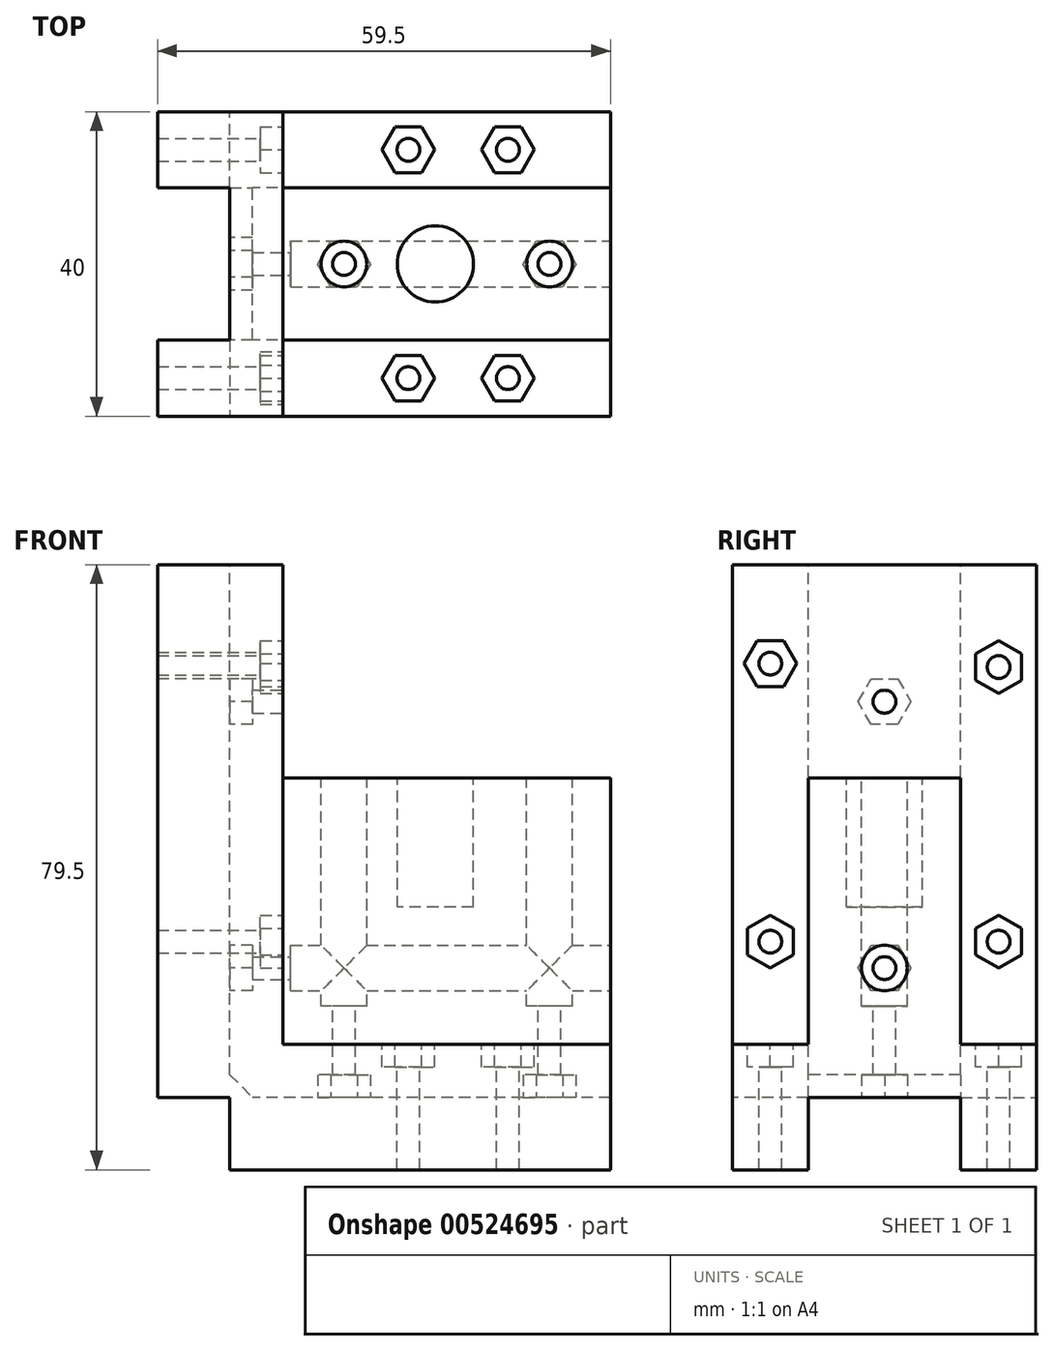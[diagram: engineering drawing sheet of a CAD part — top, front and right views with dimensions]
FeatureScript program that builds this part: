
annotation { "Feature Type Name" : "Feature", "Feature Type Description" : "" }
export const myFeature = defineFeature(function(context is Context, id is Id, definition is map)
    precondition{}
    {
        {
            var Q0;
            Q0=qCreatedBy(makeId("Front.planeOp"),FACE);
            var sketch = newSketch(context, id + "F0", { "sketchPlane" : qUnion([Q0])});
            skLineSegment(sketch, "E0", {"start": v(-50, 89.2) * mm, "end": v(-50, 19.2) * mm});
            skLineSegment(sketch, "E1", {"start": v(-50, 19.2) * mm, "end": v(0, 19.2) * mm});
            skLineSegment(sketch, "E2", {"start": v(0, 19.2) * mm, "end": v(0, 61.2) * mm});
            skLineSegment(sketch, "E3", {"start": v(0, 61.2) * mm, "end": v(-43, 61.2) * mm});
            skLineSegment(sketch, "E4", {"start": v(-43, 61.2) * mm, "end": v(-43, 89.2) * mm});
            skLineSegment(sketch, "E5", {"start": v(-43, 89.2) * mm, "end": v(-50, 89.2) * mm});
            skSolve(sketch);
        }
        {
            var Q0;
            Q0 = qSketchRegion(id + "F0", true);
            extrude(context, id + "F1", {"entities" : qUnion([Q0]), "depth" : 20 * mm, "offsetDistance" : 25 * mm});
        }
        {
            var Q0;
            Q0=makeQuery(id+"F1.opExtrude","CAP_FACE",FACE,{"disambiguationData":[OSD([sQuery(id+"F0.wireOp",EDGE,"E0"),sQuery(id+"F0.wireOp",EDGE,"E1"),sQuery(id+"F0.wireOp",EDGE,"E2"),sQuery(id+"F0.wireOp",EDGE,"E3"),sQuery(id+"F0.wireOp",EDGE,"E4"),sQuery(id+"F0.wireOp",EDGE,"E5")])],"isStart":false});
            var sketch = newSketch(context, id + "F2", { "sketchPlane" : qUnion([Q0])});
            skLineSegment(sketch, "E6", {"start": v(-50, 26.2) * mm, "end": v(0, 26.2) * mm});
            skSolve(sketch);
        }
        {
            var Q0;
            {var subQ0=sQuery(id+"F2.wireOp",EDGE,"E6");Q0=makeQuery(id+"F2.imprint","IMPRINT",FACE,{"disambiguationData":[TD([[makeQuery(id+"F2.imprint","IMPRINT",EDGE,{"derivedFrom":subQ0}),-1.0]])]});}
            extrude(context, id + "F3", {"entities" : qUnion([Q0]), "operationType" : NewBodyOperationType.ADD, "depth" : 10 * mm, "offsetDistance" : 25 * mm});
        }
        {
            var Q0;
            Q0=makeQuery(id+"F1.opExtrude","CAP_FACE",FACE,{"disambiguationData":[OSD([sQuery(id+"F0.wireOp",EDGE,"E0"),sQuery(id+"F0.wireOp",EDGE,"E1"),sQuery(id+"F0.wireOp",EDGE,"E2"),sQuery(id+"F0.wireOp",EDGE,"E3"),sQuery(id+"F0.wireOp",EDGE,"E4"),sQuery(id+"F0.wireOp",EDGE,"E5")])],"isStart":true});
            var sketch = newSketch(context, id + "F4", { "sketchPlane" : qUnion([Q0])});
            skLineSegment(sketch, "E7", {"start": v(0, 26.2) * mm, "end": v(50, 26.2) * mm});
            skSolve(sketch);
        }
        {
            var Q0;
            {var subQ0=sQuery(id+"F4.wireOp",EDGE,"E7");Q0=makeQuery(id+"F4.imprint","IMPRINT",FACE,{"disambiguationData":[TD([[makeQuery(id+"F4.imprint","IMPRINT",EDGE,{"derivedFrom":subQ0}),-1.0]])]});}
            extrude(context, id + "F5", {"entities" : qUnion([Q0]), "operationType" : NewBodyOperationType.ADD, "depth" : 10 * mm, "offsetDistance" : 25 * mm});
        }
        {
            var Q0;
            {var subQ0=sQuery(id+"F0.wireOp",EDGE,"E1");Q0=makeQuery(id+"F5.boolean.opBoolean","MERGE",FACE,{"derivedFrom":[makeQuery(id+"F3.boolean.opBoolean","MERGE",FACE,{"derivedFrom":[makeQuery(id+"F1.opExtrude","SWEPT_FACE",FACE,{"disambiguationData":[OSD([subQ0])]}),makeQuery(id+"F3.opExtrude","SWEPT_FACE",FACE,{"disambiguationData":[OSD([subQ0])]})]}),makeQuery(id+"F5.opExtrude","SWEPT_FACE",FACE,{"disambiguationData":[OSD([subQ0])]})]});}
            var sketch = newSketch(context, id + "F6", { "sketchPlane" : qUnion([Q0])});
            skLineSegment(sketch, "E8", {"start": v(0, 20) * mm, "end": v(-50, 20) * mm});
            skLineSegment(sketch, "E9", {"start": v(0, 0) * mm, "end": v(-50, 0) * mm});
            skSolve(sketch);
        }
        {
            var Q0;
            {var subQ0=sQuery(id+"F6.wireOp",EDGE,"E8");Q0=makeQuery(id+"F6.imprint","IMPRINT",FACE,{"disambiguationData":[TD([[makeQuery(id+"F6.imprint","IMPRINT",EDGE,{"derivedFrom":subQ0}),-1.0]])]});}
            var Q1;
            {var subQ0=sQuery(id+"F6.wireOp",EDGE,"E9");Q1=makeQuery(id+"F6.imprint","IMPRINT",FACE,{"disambiguationData":[TD([[makeQuery(id+"F6.imprint","IMPRINT",EDGE,{"derivedFrom":subQ0}),1.0]])]});}
            extrude(context, id + "F7", {"entities" : qUnion([Q0, Q1]), "operationType" : NewBodyOperationType.ADD, "depth" : 9.5 * mm, "offsetDistance" : 25 * mm});
        }
        {
            var Q0;
            Q0=makeQuery(id+"F5.opExtrude","SWEPT_FACE",FACE,{"disambiguationData":[OSD([sQuery(id+"F4.wireOp",EDGE,"E7")])]});
            var sketch = newSketch(context, id + "F8", { "sketchPlane" : qUnion([Q0])});
            skLineSegment(sketch, "E10", {"start": v(-30, -25) * mm, "end": v(-28.27, -28) * mm});
            skLineSegment(sketch, "E11", {"start": v(-28.27, -28) * mm, "end": v(-24.8, -28) * mm});
            skLineSegment(sketch, "E12", {"start": v(-24.8, -28) * mm, "end": v(-23.07, -25) * mm});
            skLineSegment(sketch, "E13", {"start": v(-23.07, -25) * mm, "end": v(-24.8, -22) * mm});
            skLineSegment(sketch, "E14", {"start": v(-24.8, -22) * mm, "end": v(-28.27, -22) * mm});
            skLineSegment(sketch, "E15", {"start": v(-28.27, -22) * mm, "end": v(-30, -25) * mm});
            skCircle(sketch, "E16", {"center": v(-26.54, -25) * mm, "radius": 1.5 * mm});
            skLineSegment(sketch, "E17", {"start": v(-16.93, -25) * mm, "end": v(-15.2, -28) * mm});
            skLineSegment(sketch, "E18", {"start": v(-15.2, -28) * mm, "end": v(-11.73, -28) * mm});
            skLineSegment(sketch, "E19", {"start": v(-11.73, -28) * mm, "end": v(-10, -25) * mm});
            skLineSegment(sketch, "E20", {"start": v(-10, -25) * mm, "end": v(-11.73, -22) * mm});
            skLineSegment(sketch, "E21", {"start": v(-11.73, -22) * mm, "end": v(-15.2, -22) * mm});
            skLineSegment(sketch, "E22", {"start": v(-15.2, -22) * mm, "end": v(-16.93, -25) * mm});
            skCircle(sketch, "E23", {"center": v(-13.46, -25) * mm, "radius": 1.5 * mm});
            skLineSegment(sketch, "E24", {"start": v(-30, 5) * mm, "end": v(-28.27, 2) * mm});
            skLineSegment(sketch, "E25", {"start": v(-28.27, 2) * mm, "end": v(-24.8, 2) * mm});
            skLineSegment(sketch, "E26", {"start": v(-24.8, 2) * mm, "end": v(-23.07, 5) * mm});
            skLineSegment(sketch, "E27", {"start": v(-23.07, 5) * mm, "end": v(-24.8, 8) * mm});
            skLineSegment(sketch, "E28", {"start": v(-24.8, 8) * mm, "end": v(-28.27, 8) * mm});
            skLineSegment(sketch, "E29", {"start": v(-28.27, 8) * mm, "end": v(-30, 5) * mm});
            skCircle(sketch, "E30", {"center": v(-26.54, 5) * mm, "radius": 1.5 * mm});
            skLineSegment(sketch, "E31", {"start": v(-16.93, 5) * mm, "end": v(-15.2, 2) * mm});
            skLineSegment(sketch, "E32", {"start": v(-15.2, 2) * mm, "end": v(-11.73, 2) * mm});
            skLineSegment(sketch, "E33", {"start": v(-11.73, 2) * mm, "end": v(-10, 5) * mm});
            skLineSegment(sketch, "E34", {"start": v(-10, 5) * mm, "end": v(-11.73, 8) * mm});
            skLineSegment(sketch, "E35", {"start": v(-11.73, 8) * mm, "end": v(-15.2, 8) * mm});
            skLineSegment(sketch, "E36", {"start": v(-15.2, 8) * mm, "end": v(-16.93, 5) * mm});
            skCircle(sketch, "E37", {"center": v(-13.46, 5) * mm, "radius": 1.5 * mm});
            skLineSegment(sketch, "E38", {"start": v(-43, 0) * mm, "end": v(-43, 10) * mm});
            skLineSegment(sketch, "E39.bottom", {"start": v(-43, -20) * mm, "end": v(-50, -20) * mm});
            skLineSegment(sketch, "E39.top", {"start": v(-43, -30) * mm, "end": v(-50, -30) * mm});
            skLineSegment(sketch, "E39.left", {"start": v(-43, -20) * mm, "end": v(-43, -30) * mm});
            skLineSegment(sketch, "E39.right", {"start": v(-50, -20) * mm, "end": v(-50, -30) * mm});
            skSolve(sketch);
        }
        {
            var Q0;
            Q0=makeQuery(id+"F8.imprint","IMPRINT",FACE,{"disambiguationData":[TD([[makeQuery(id+"F8.imprint","IMPRINT",EDGE,{"derivedFrom":sQuery(id+"F8.wireOp",EDGE,"E24")}),1.0]])]});
            var Q1;
            Q1=makeQuery(id+"F8.imprint","IMPRINT",FACE,{"disambiguationData":[TD([[makeQuery(id+"F8.imprint","IMPRINT",EDGE,{"derivedFrom":sQuery(id+"F8.wireOp",EDGE,"E31")}),1.0]])]});
            var Q2;
            Q2=makeQuery(id+"F8.imprint","IMPRINT",FACE,{"disambiguationData":[TD([[makeQuery(id+"F8.imprint","IMPRINT",EDGE,{"derivedFrom":sQuery(id+"F8.wireOp",EDGE,"E17")}),1.0]])]});
            var Q3;
            Q3=makeQuery(id+"F8.imprint","IMPRINT",FACE,{"disambiguationData":[TD([[makeQuery(id+"F8.imprint","IMPRINT",EDGE,{"derivedFrom":sQuery(id+"F8.wireOp",EDGE,"E10")}),1.0]])]});
            extrude(context, id + "F9", {"entities" : qUnion([Q0, Q1, Q2, Q3]), "operationType" : NewBodyOperationType.REMOVE, "oppositeDirection" : true, "depth" : 3 * mm, "offsetDistance" : 25 * mm});
        }
        {
            var Q0;
            Q0=makeQuery(id+"F9.boolean.opBoolean","SPLIT",FACE,{"disambiguationData":[TD([makeQuery(id+"F9.opExtrude","SWEPT_FACE",FACE,{"disambiguationData":[OSD([sQuery(id+"F8.wireOp",EDGE,"E30")])]})])],"derivedFrom":makeQuery(id+"F5.opExtrude","SWEPT_FACE",FACE,{"disambiguationData":[OSD([sQuery(id+"F4.wireOp",EDGE,"E7")])]})});
            var Q1;
            Q1=makeQuery(id+"F9.boolean.opBoolean","SPLIT",FACE,{"disambiguationData":[TD([makeQuery(id+"F9.opExtrude","SWEPT_FACE",FACE,{"disambiguationData":[OSD([sQuery(id+"F8.wireOp",EDGE,"E16")])]})])],"derivedFrom":makeQuery(id+"F3.opExtrude","SWEPT_FACE",FACE,{"disambiguationData":[OSD([sQuery(id+"F2.wireOp",EDGE,"E6")])]})});
            var Q2;
            Q2=makeQuery(id+"F9.boolean.opBoolean","SPLIT",FACE,{"disambiguationData":[TD([makeQuery(id+"F9.opExtrude","SWEPT_FACE",FACE,{"disambiguationData":[OSD([sQuery(id+"F8.wireOp",EDGE,"E23")])]})])],"derivedFrom":makeQuery(id+"F3.opExtrude","SWEPT_FACE",FACE,{"disambiguationData":[OSD([sQuery(id+"F2.wireOp",EDGE,"E6")])]})});
            var Q3;
            Q3=makeQuery(id+"F9.boolean.opBoolean","SPLIT",FACE,{"disambiguationData":[TD([makeQuery(id+"F9.opExtrude","SWEPT_FACE",FACE,{"disambiguationData":[OSD([sQuery(id+"F8.wireOp",EDGE,"E37")])]})])],"derivedFrom":makeQuery(id+"F5.opExtrude","SWEPT_FACE",FACE,{"disambiguationData":[OSD([sQuery(id+"F4.wireOp",EDGE,"E7")])]})});
            extrude(context, id + "F10", {"entities" : qUnion([Q0, Q1, Q2, Q3]), "operationType" : NewBodyOperationType.REMOVE, "oppositeDirection" : true, "depth" : 20 * mm, "offsetDistance" : 25 * mm});
        }
        {
            var Q0;
            {var subQ0=sQuery(id+"F8.wireOp",EDGE,"E38");Q0=makeQuery(id+"F8.imprint","IMPRINT",FACE,{"disambiguationData":[TD([[makeQuery(id+"F8.imprint","IMPRINT",EDGE,{"derivedFrom":subQ0}),1.0]])]});}
            var Q1;
            Q1=makeQuery(id+"F8.imprint","IMPRINT",FACE,{"disambiguationData":[TD([[makeQuery(id+"F8.imprint","IMPRINT",EDGE,{"derivedFrom":sQuery(id+"F8.wireOp",EDGE,"E39.bottom")}),1.0]])]});
            extrude(context, id + "F11", {"entities" : qUnion([Q0, Q1]), "operationType" : NewBodyOperationType.ADD, "depth" : 63 * mm, "offsetDistance" : 25 * mm});
        }
        {
            var Q0;
            {var subQ0=sQuery(id+"F0.wireOp",EDGE,"E0");var subQ1=sQuery(id+"F0.wireOp",EDGE,"E1");var subQ2=makeQuery(id+"F5.boolean.opBoolean","MERGE",EDGE,{"derivedFrom":[makeQuery(id+"F3.boolean.opBoolean","MERGE",EDGE,{"derivedFrom":[makeQuery(id+"F1.opExtrude","SWEPT_EDGE",EDGE,{"disambiguationData":[OSD([subQ0,subQ1])]}),makeQuery(id+"F3.opExtrude","SWEPT_EDGE",EDGE,{"disambiguationData":[OSD([subQ0,subQ1])]})]}),makeQuery(id+"F5.opExtrude","SWEPT_EDGE",EDGE,{"disambiguationData":[OSD([subQ0,subQ1])]})]});Q0=makeQuery(id+"F11.boolean.opBoolean","MERGE",FACE,{"derivedFrom":[makeQuery(id+"F7.boolean.opBoolean","MERGE",FACE,{"derivedFrom":[makeQuery(id+"F5.boolean.opBoolean","MERGE",FACE,{"derivedFrom":[makeQuery(id+"F3.boolean.opBoolean","MERGE",FACE,{"derivedFrom":[makeQuery(id+"F1.opExtrude","SWEPT_FACE",FACE,{"disambiguationData":[OSD([subQ0])]}),makeQuery(id+"F3.opExtrude","SWEPT_FACE",FACE,{"disambiguationData":[OSD([subQ0])]})]}),makeQuery(id+"F5.opExtrude","SWEPT_FACE",FACE,{"disambiguationData":[OSD([subQ0])]})]}),makeQuery(id+"F7.opExtrude","SWEPT_FACE",FACE,{"disambiguationData":[OSD([subQ0,subQ1]),TDD([makeQuery(id+"F6.imprint","IMPRINT",EDGE,{"disambiguationData":[TD([[makeQuery(id+"F6.imprint","INTERSECT",VERTEX,{"derivedFrom":[makeQuery(id+"F3.opExtrude","CAP_EDGE",EDGE,{"disambiguationData":[OSD([subQ1])],"isStart":false}),subQ2]}),-1.0]])],"derivedFrom":subQ2})])]}),makeQuery(id+"F7.opExtrude","SWEPT_FACE",FACE,{"disambiguationData":[OSD([subQ0,subQ1]),TDD([makeQuery(id+"F6.imprint","IMPRINT",EDGE,{"disambiguationData":[TD([[makeQuery(id+"F6.imprint","INTERSECT",VERTEX,{"derivedFrom":[makeQuery(id+"F5.opExtrude","CAP_EDGE",EDGE,{"disambiguationData":[OSD([subQ1])],"isStart":false}),subQ2]}),1.0]])],"derivedFrom":subQ2})])]})]}),makeQuery(id+"F11.opExtrude","SWEPT_FACE",FACE,{"disambiguationData":[OSD([sQuery(id+"F8.wireOp",EDGE,"E39.right")])]}),makeQuery(id+"F11.opExtrude","SWEPT_FACE",FACE,{"disambiguationData":[OSD([subQ0,sQuery(id+"F4.wireOp",EDGE,"E7")])]})]});}
            var sketch = newSketch(context, id + "F12", { "sketchPlane" : qUnion([Q0])});
            skLineSegment(sketch, "E40", {"start": v(20, 19.2) * mm, "end": v(20, 89.2) * mm});
            skLineSegment(sketch, "E41", {"start": v(0, 19.2) * mm, "end": v(0, 89.2) * mm});
            skLineSegment(sketch, "E42", {"start": v(20, 19.2) * mm, "end": v(30, 19.2) * mm});
            skLineSegment(sketch, "E43", {"start": v(0, 19.2) * mm, "end": v(-10, 19.2) * mm});
            skSolve(sketch);
        }
        {
            var Q0;
            {var subQ0=sQuery(id+"F12.wireOp",EDGE,"E40");Q0=makeQuery(id+"F12.imprint","IMPRINT",FACE,{"disambiguationData":[TD([[makeQuery(id+"F12.imprint","IMPRINT",EDGE,{"derivedFrom":subQ0}),-1.0]])]});}
            var Q1;
            {var subQ0=sQuery(id+"F12.wireOp",EDGE,"E41");Q1=makeQuery(id+"F12.imprint","IMPRINT",FACE,{"disambiguationData":[TD([[makeQuery(id+"F12.imprint","IMPRINT",EDGE,{"derivedFrom":subQ0}),1.0]])]});}
            extrude(context, id + "F13", {"entities" : qUnion([Q0, Q1]), "operationType" : NewBodyOperationType.ADD, "depth" : 9.5 * mm, "offsetDistance" : 25 * mm});
        }
        {
            var Q0;
            Q0=makeQuery(id+"F11.opExtrude","SWEPT_FACE",FACE,{"disambiguationData":[OSD([sQuery(id+"F8.wireOp",EDGE,"E39.left")])]});
            var sketch = newSketch(context, id + "F14", { "sketchPlane" : qUnion([Q0])});
            skLineSegment(sketch, "E44", {"start": v(-25, 43.12) * mm, "end": v(-28, 41.39) * mm});
            skLineSegment(sketch, "E45", {"start": v(-28, 41.39) * mm, "end": v(-28, 37.93) * mm});
            skLineSegment(sketch, "E46", {"start": v(-28, 37.93) * mm, "end": v(-25, 36.2) * mm});
            skLineSegment(sketch, "E47", {"start": v(-25, 36.2) * mm, "end": v(-22, 37.93) * mm});
            skLineSegment(sketch, "E48", {"start": v(-22, 37.93) * mm, "end": v(-22, 41.39) * mm});
            skLineSegment(sketch, "E49", {"start": v(-22, 41.39) * mm, "end": v(-25, 43.12) * mm});
            skCircle(sketch, "E50", {"center": v(-25, 39.66) * mm, "radius": 1.5 * mm});
            skLineSegment(sketch, "E51", {"start": v(5, 79.2) * mm, "end": v(2, 77.46) * mm});
            skLineSegment(sketch, "E52", {"start": v(2, 77.46) * mm, "end": v(2, 74) * mm});
            skLineSegment(sketch, "E53", {"start": v(2, 74) * mm, "end": v(5, 72.26) * mm});
            skLineSegment(sketch, "E54", {"start": v(5, 72.26) * mm, "end": v(8, 74) * mm});
            skLineSegment(sketch, "E55", {"start": v(8, 74) * mm, "end": v(8, 77.46) * mm});
            skLineSegment(sketch, "E56", {"start": v(8, 77.46) * mm, "end": v(5, 79.2) * mm});
            skCircle(sketch, "E57", {"center": v(5, 75.73) * mm, "radius": 1.5 * mm});
            skLineSegment(sketch, "E58", {"start": v(5, 43.12) * mm, "end": v(2, 41.39) * mm});
            skLineSegment(sketch, "E59", {"start": v(2, 41.39) * mm, "end": v(2, 37.93) * mm});
            skLineSegment(sketch, "E60", {"start": v(2, 37.93) * mm, "end": v(5, 36.2) * mm});
            skLineSegment(sketch, "E61", {"start": v(5, 36.2) * mm, "end": v(8, 37.93) * mm});
            skLineSegment(sketch, "E62", {"start": v(8, 37.93) * mm, "end": v(8, 41.39) * mm});
            skLineSegment(sketch, "E63", {"start": v(8, 41.39) * mm, "end": v(5, 43.12) * mm});
            skCircle(sketch, "E64", {"center": v(5, 39.66) * mm, "radius": 1.5 * mm});
            skLineSegment(sketch, "E65", {"start": v(-28.46, 76.2) * mm, "end": v(-26.73, 73.2) * mm});
            skLineSegment(sketch, "E66", {"start": v(-26.73, 73.2) * mm, "end": v(-23.27, 73.2) * mm});
            skLineSegment(sketch, "E67", {"start": v(-23.27, 73.2) * mm, "end": v(-21.54, 76.2) * mm});
            skLineSegment(sketch, "E68", {"start": v(-21.54, 76.2) * mm, "end": v(-23.27, 79.2) * mm});
            skLineSegment(sketch, "E69", {"start": v(-23.27, 79.2) * mm, "end": v(-26.73, 79.2) * mm});
            skLineSegment(sketch, "E70", {"start": v(-26.73, 79.2) * mm, "end": v(-28.46, 76.2) * mm});
            skCircle(sketch, "E71", {"center": v(-25, 76.2) * mm, "radius": 1.5 * mm});
            skSolve(sketch);
        }
        {
            var Q0;
            Q0=makeQuery(id+"F14.imprint","IMPRINT",FACE,{"disambiguationData":[TD([[makeQuery(id+"F14.imprint","IMPRINT",EDGE,{"derivedFrom":sQuery(id+"F14.wireOp",EDGE,"3def0d78-31c6-4fae-8652-5ddfac95fd14")}),1.0]])]});
            var Q1;
            Q1=makeQuery(id+"F14.imprint","IMPRINT",FACE,{"disambiguationData":[TD([[makeQuery(id+"F14.imprint","IMPRINT",EDGE,{"derivedFrom":sQuery(id+"F14.wireOp",EDGE,"E51")}),1.0]])]});
            var Q2;
            Q2=makeQuery(id+"F14.imprint","IMPRINT",FACE,{"disambiguationData":[TD([[makeQuery(id+"F14.imprint","IMPRINT",EDGE,{"derivedFrom":sQuery(id+"F14.wireOp",EDGE,"E44")}),1.0]])]});
            var Q3;
            Q3=makeQuery(id+"F14.imprint","IMPRINT",FACE,{"disambiguationData":[TD([[makeQuery(id+"F14.imprint","IMPRINT",EDGE,{"derivedFrom":sQuery(id+"F14.wireOp",EDGE,"E58")}),1.0]])]});
            var Q4;
            Q4 = qSketchRegion(id + "F17", true);
            var Q5;
            Q5=makeQuery(id+"F14.imprint","IMPRINT",FACE,{"disambiguationData":[TD([[makeQuery(id+"F14.imprint","IMPRINT",EDGE,{"derivedFrom":sQuery(id+"F14.wireOp",EDGE,"E65")}),1.0]])]});
            extrude(context, id + "F15", {"entities" : qUnion([Q0, Q1, Q2, Q3, Q4, Q5]), "operationType" : NewBodyOperationType.REMOVE, "oppositeDirection" : true, "depth" : 3 * mm, "offsetDistance" : 25 * mm});
        }
        {
            var Q0;
            Q0=makeQuery(id+"F15.boolean.opBoolean","SPLIT",FACE,{"disambiguationData":[TD([makeQuery(id+"F15.opExtrude","SWEPT_FACE",FACE,{"disambiguationData":[OSD([sQuery(id+"F14.wireOp",EDGE,"ef229b5c-997c-4e16-8a30-6795fe06fc26")])]})])],"derivedFrom":makeQuery(id+"F11.opExtrude","SWEPT_FACE",FACE,{"disambiguationData":[OSD([sQuery(id+"F8.wireOp",EDGE,"E39.left")])]})});
            var Q1;
            Q1=makeQuery(id+"F15.boolean.opBoolean","SPLIT",FACE,{"disambiguationData":[TD([makeQuery(id+"F15.opExtrude","SWEPT_FACE",FACE,{"disambiguationData":[OSD([sQuery(id+"F14.wireOp",EDGE,"E57")])]})])],"derivedFrom":makeQuery(id+"F11.opExtrude","SWEPT_FACE",FACE,{"disambiguationData":[OSD([sQuery(id+"F8.wireOp",EDGE,"E38")])]})});
            var Q2;
            Q2=makeQuery(id+"F15.boolean.opBoolean","SPLIT",FACE,{"disambiguationData":[TD([makeQuery(id+"F15.opExtrude","SWEPT_FACE",FACE,{"disambiguationData":[OSD([sQuery(id+"F14.wireOp",EDGE,"E64")])]})])],"derivedFrom":makeQuery(id+"F11.opExtrude","SWEPT_FACE",FACE,{"disambiguationData":[OSD([sQuery(id+"F8.wireOp",EDGE,"E38")])]})});
            var Q3;
            Q3=makeQuery(id+"F15.boolean.opBoolean","SPLIT",FACE,{"disambiguationData":[TD([makeQuery(id+"F15.opExtrude","SWEPT_FACE",FACE,{"disambiguationData":[OSD([sQuery(id+"F14.wireOp",EDGE,"E50")])]})])],"derivedFrom":makeQuery(id+"F11.opExtrude","SWEPT_FACE",FACE,{"disambiguationData":[OSD([sQuery(id+"F8.wireOp",EDGE,"E39.left")])]})});
            var Q4;
            Q4=makeQuery(id+"F15.boolean.opBoolean","SPLIT",FACE,{"disambiguationData":[TD([makeQuery(id+"F15.opExtrude","SWEPT_FACE",FACE,{"disambiguationData":[OSD([sQuery(id+"F14.wireOp",EDGE,"E71")])]})])],"derivedFrom":makeQuery(id+"F11.boolean.opBoolean","MERGE",FACE,{"derivedFrom":[makeQuery(id+"F1.opExtrude","SWEPT_FACE",FACE,{"disambiguationData":[OSD([sQuery(id+"F0.wireOp",EDGE,"E4")])]}),makeQuery(id+"F11.opExtrude","SWEPT_FACE",FACE,{"disambiguationData":[OSD([sQuery(id+"F8.wireOp",EDGE,"E38")])]}),makeQuery(id+"F11.opExtrude","SWEPT_FACE",FACE,{"disambiguationData":[OSD([sQuery(id+"F8.wireOp",EDGE,"E39.left")])]})]})});
            extrude(context, id + "F16", {"entities" : qUnion([Q0, Q1, Q2, Q3, Q4]), "operationType" : NewBodyOperationType.REMOVE, "oppositeDirection" : true, "depth" : 20 * mm, "offsetDistance" : 25 * mm});
        }
        {
            var Q0;
            Q0=makeQuery(id+"F1.opExtrude","SWEPT_FACE",FACE,{"disambiguationData":[OSD([sQuery(id+"F0.wireOp",EDGE,"E3")])]});
            var sketch = newSketch(context, id + "F17", { "sketchPlane" : qUnion([Q0])});
            skCircle(sketch, "E72", {"center": v(-23, -10) * mm, "radius": 5 * mm});
            skPoint(sketch, "E73", {"position": v(-8, -10) * mm});
            skPoint(sketch, "E74", {"position": v(-35, -10) * mm});
            skSolve(sketch);
        }
        {
            var Q0;
            Q0=makeQuery(id+"F17.imprint","IMPRINT",FACE,{"disambiguationData":[TD([[makeQuery(id+"F17.imprint","IMPRINT",EDGE,{"derivedFrom":sQuery(id+"F17.wireOp",EDGE,"E72")}),1.0]])]});
            extrude(context, id + "F18", {"entities" : qUnion([Q0]), "operationType" : NewBodyOperationType.REMOVE, "oppositeDirection" : true, "depth" : 17 * mm, "offsetDistance" : 25 * mm});
        }
        {
            var Q0;
            {var subQ0=sQuery(id+"F0.wireOp",EDGE,"E1");var subQ1=sQuery(id+"F0.wireOp",EDGE,"E0");Q0=makeQuery(id+"F5.boolean.opBoolean","MERGE",EDGE,{"derivedFrom":[makeQuery(id+"F3.boolean.opBoolean","MERGE",EDGE,{"derivedFrom":[makeQuery(id+"F1.opExtrude","SWEPT_EDGE",EDGE,{"disambiguationData":[OSD([subQ1,subQ0])]}),makeQuery(id+"F3.opExtrude","SWEPT_EDGE",EDGE,{"disambiguationData":[OSD([subQ1,subQ0])]})]}),makeQuery(id+"F5.opExtrude","SWEPT_EDGE",EDGE,{"disambiguationData":[OSD([subQ1,subQ0])]})]});}
            chamfer(context, id + "F19", {"entities" : qUnion([Q0]), "width" : 3 * mm, "tangentPropagation" : true});
        }
        {
            var Q0;
            Q0=sQuery(id+"F17.wireOp",VERTEX,"E73");
            var Q1;
            Q1=sQuery(id+"F17.wireOp",VERTEX,"E74");
            var Q2;
            Q2=makeQuery(id+"F1.opExtrude","SWEPT_BODY",BODY,{"disambiguationData":[OSD([sQuery(id+"F0.wireOp",EDGE,"E0"),sQuery(id+"F0.wireOp",EDGE,"E1"),sQuery(id+"F0.wireOp",EDGE,"E2"),sQuery(id+"F0.wireOp",EDGE,"E3"),sQuery(id+"F0.wireOp",EDGE,"E4"),sQuery(id+"F0.wireOp",EDGE,"E5")])]});
            hole(context, id + "F20", {"style" : HoleStyle.C_BORE, "endStyle" : HoleEndStyle.THROUGH, "holeDiameter" : 3 * mm, "cBoreDiameter" : 6 * mm, "cBoreDepth" : 30 * mm, "isTappedThrough" : true, "tappedDepth" : 12 * mm, "tapClearance" : 3, "startFromSketch" : true, "locations" : qUnion([Q0, Q1]), "scope" : qUnion([Q2])});
        }
        {
            var Q0;
            {var subQ0=sQuery(id+"F0.wireOp",EDGE,"E1");Q0=makeQuery(id+"F5.boolean.opBoolean","MERGE",FACE,{"derivedFrom":[makeQuery(id+"F3.boolean.opBoolean","MERGE",FACE,{"derivedFrom":[makeQuery(id+"F1.opExtrude","SWEPT_FACE",FACE,{"disambiguationData":[OSD([subQ0])]}),makeQuery(id+"F3.opExtrude","SWEPT_FACE",FACE,{"disambiguationData":[OSD([subQ0])]})]}),makeQuery(id+"F5.opExtrude","SWEPT_FACE",FACE,{"disambiguationData":[OSD([subQ0])]})]});}
            var sketch = newSketch(context, id + "F21", { "sketchPlane" : qUnion([Q0])});
            skLineSegment(sketch, "E75", {"start": v(-38.46, 10) * mm, "end": v(-36.73, 7) * mm});
            skLineSegment(sketch, "E76", {"start": v(-36.73, 7) * mm, "end": v(-33.27, 7) * mm});
            skLineSegment(sketch, "E77", {"start": v(-33.27, 7) * mm, "end": v(-31.54, 10) * mm});
            skLineSegment(sketch, "E78", {"start": v(-31.54, 10) * mm, "end": v(-33.27, 13) * mm});
            skLineSegment(sketch, "E79", {"start": v(-33.27, 13) * mm, "end": v(-36.73, 13) * mm});
            skLineSegment(sketch, "E80", {"start": v(-36.73, 13) * mm, "end": v(-38.46, 10) * mm});
            skCircle(sketch, "E81", {"center": v(-35, 10) * mm, "radius": 1.5 * mm});
            skLineSegment(sketch, "E82", {"start": v(-11.46, 10) * mm, "end": v(-9.73, 7) * mm});
            skLineSegment(sketch, "E83", {"start": v(-9.73, 7) * mm, "end": v(-6.27, 7) * mm});
            skLineSegment(sketch, "E84", {"start": v(-6.27, 7) * mm, "end": v(-4.54, 10) * mm});
            skLineSegment(sketch, "E85", {"start": v(-4.54, 10) * mm, "end": v(-6.27, 13) * mm});
            skLineSegment(sketch, "E86", {"start": v(-6.27, 13) * mm, "end": v(-9.73, 13) * mm});
            skLineSegment(sketch, "E87", {"start": v(-9.73, 13) * mm, "end": v(-11.46, 10) * mm});
            skCircle(sketch, "E88", {"center": v(-8, 10) * mm, "radius": 1.5 * mm});
            skSolve(sketch);
        }
        {
            var Q0;
            Q0=makeQuery(id+"F21.imprint","IMPRINT",FACE,{"disambiguationData":[TD([[makeQuery(id+"F21.imprint","IMPRINT",EDGE,{"derivedFrom":sQuery(id+"F21.wireOp",EDGE,"E75")}),1.0]])]});
            var Q1;
            Q1=makeQuery(id+"F21.imprint","IMPRINT",FACE,{"disambiguationData":[TD([[makeQuery(id+"F21.imprint","IMPRINT",EDGE,{"derivedFrom":sQuery(id+"F21.wireOp",EDGE,"E82")}),1.0]])]});
            extrude(context, id + "F22", {"entities" : qUnion([Q0, Q1]), "operationType" : NewBodyOperationType.REMOVE, "oppositeDirection" : true, "depth" : 3 * mm, "offsetDistance" : 25 * mm});
        }
        {
            var Q0;
            {var subQ0=sQuery(id+"F0.wireOp",EDGE,"E2");var subQ1=sQuery(id+"F0.wireOp",EDGE,"E1");var subQ2=makeQuery(id+"F5.boolean.opBoolean","MERGE",EDGE,{"derivedFrom":[makeQuery(id+"F3.boolean.opBoolean","MERGE",EDGE,{"derivedFrom":[makeQuery(id+"F1.opExtrude","SWEPT_EDGE",EDGE,{"disambiguationData":[OSD([subQ1,subQ0])]}),makeQuery(id+"F3.opExtrude","SWEPT_EDGE",EDGE,{"disambiguationData":[OSD([subQ1,subQ0])]})]}),makeQuery(id+"F5.opExtrude","SWEPT_EDGE",EDGE,{"disambiguationData":[OSD([subQ1,subQ0])]})]});Q0=makeQuery(id+"F7.boolean.opBoolean","MERGE",FACE,{"derivedFrom":[makeQuery(id+"F5.boolean.opBoolean","MERGE",FACE,{"derivedFrom":[makeQuery(id+"F3.boolean.opBoolean","MERGE",FACE,{"derivedFrom":[makeQuery(id+"F1.opExtrude","SWEPT_FACE",FACE,{"disambiguationData":[OSD([subQ0])]}),makeQuery(id+"F3.opExtrude","SWEPT_FACE",FACE,{"disambiguationData":[OSD([subQ0])]})]}),makeQuery(id+"F5.opExtrude","SWEPT_FACE",FACE,{"disambiguationData":[OSD([subQ0])]})]}),makeQuery(id+"F7.opExtrude","SWEPT_FACE",FACE,{"disambiguationData":[OSD([subQ1,subQ0]),TDD([makeQuery(id+"F6.imprint","IMPRINT",EDGE,{"disambiguationData":[TD([[makeQuery(id+"F6.imprint","INTERSECT",VERTEX,{"derivedFrom":[makeQuery(id+"F3.opExtrude","CAP_EDGE",EDGE,{"disambiguationData":[OSD([subQ1])],"isStart":false}),subQ2]}),-1.0]])],"derivedFrom":subQ2})])]}),makeQuery(id+"F7.opExtrude","SWEPT_FACE",FACE,{"disambiguationData":[OSD([subQ1,subQ0]),TDD([makeQuery(id+"F6.imprint","IMPRINT",EDGE,{"disambiguationData":[TD([[makeQuery(id+"F6.imprint","INTERSECT",VERTEX,{"derivedFrom":[makeQuery(id+"F5.opExtrude","CAP_EDGE",EDGE,{"disambiguationData":[OSD([subQ1])],"isStart":false}),subQ2]}),1.0]])],"derivedFrom":subQ2})])]})]});}
            var sketch = newSketch(context, id + "F23", { "sketchPlane" : qUnion([Q0])});
            skPoint(sketch, "E89", {"position": v(-10, 36.2) * mm});
            skSolve(sketch);
        }
        {
            var Q0;
            {var subQ4=sQuery(id+"F0.wireOp",EDGE,"E4");var subQ5=sQuery(id+"F0.wireOp",EDGE,"E3");var subQ15=sQuery(id+"F8.wireOp",EDGE,"E38");var subQ17=sQuery(id+"F8.wireOp",EDGE,"E39.left");Q0=makeQuery(id+"F15.boolean.opBoolean","SPLIT",FACE,{"disambiguationData":[TD([makeQuery(id+"F1.opExtrude","SWEPT_FACE",FACE,{"disambiguationData":[OSD([subQ5])]})])],"derivedFrom":makeQuery(id+"F11.boolean.opBoolean","MERGE",FACE,{"derivedFrom":[makeQuery(id+"F1.opExtrude","SWEPT_FACE",FACE,{"disambiguationData":[OSD([subQ4])]}),makeQuery(id+"F11.opExtrude","SWEPT_FACE",FACE,{"disambiguationData":[OSD([subQ15])]}),makeQuery(id+"F11.opExtrude","SWEPT_FACE",FACE,{"disambiguationData":[OSD([subQ17])]})]})});}
            var sketch = newSketch(context, id + "F24", { "sketchPlane" : qUnion([Q0])});
            skPoint(sketch, "E90", {"position": v(-10, 71.2) * mm});
            skSolve(sketch);
        }
        {
            var Q0;
            Q0=sQuery(id+"F24.wireOp",VERTEX,"E90");
            var Q1;
            Q1=makeQuery(id+"F1.opExtrude","SWEPT_BODY",BODY,{"disambiguationData":[OSD([sQuery(id+"F0.wireOp",EDGE,"E0"),sQuery(id+"F0.wireOp",EDGE,"E1"),sQuery(id+"F0.wireOp",EDGE,"E2"),sQuery(id+"F0.wireOp",EDGE,"E3"),sQuery(id+"F0.wireOp",EDGE,"E4"),sQuery(id+"F0.wireOp",EDGE,"E5")])]});
            hole(context, id + "F25", {"style" : HoleStyle.SIMPLE, "endStyle" : HoleEndStyle.THROUGH, "holeDiameter" : 3 * mm, "isTappedThrough" : true, "tappedDepth" : 12 * mm, "tapClearance" : 3, "startFromSketch" : true, "locations" : qUnion([Q0]), "scope" : qUnion([Q1])});
        }
        {
            var Q0;
            {var subQ0=sQuery(id+"F0.wireOp",EDGE,"E1");var subQ1=sQuery(id+"F0.wireOp",EDGE,"E0");var subQ2=makeQuery(id+"F5.boolean.opBoolean","MERGE",EDGE,{"derivedFrom":[makeQuery(id+"F3.boolean.opBoolean","MERGE",EDGE,{"derivedFrom":[makeQuery(id+"F1.opExtrude","SWEPT_EDGE",EDGE,{"disambiguationData":[OSD([subQ1,subQ0])]}),makeQuery(id+"F3.opExtrude","SWEPT_EDGE",EDGE,{"disambiguationData":[OSD([subQ1,subQ0])]})]}),makeQuery(id+"F5.opExtrude","SWEPT_EDGE",EDGE,{"disambiguationData":[OSD([subQ1,subQ0])]})]});var subQ3=makeQuery(id+"F6.imprint","INTERSECT",VERTEX,{"derivedFrom":[makeQuery(id+"F3.opExtrude","CAP_EDGE",EDGE,{"disambiguationData":[OSD([subQ0])],"isStart":false}),subQ2]});var subQ5=makeQuery(id+"F7.opExtrude","SWEPT_FACE",FACE,{"disambiguationData":[OSD([subQ1,subQ0]),TDD([makeQuery(id+"F6.imprint","IMPRINT",EDGE,{"disambiguationData":[TD([[subQ3,-1.0]])],"derivedFrom":subQ2})])]});var subQ6=makeQuery(id+"F5.opExtrude","SWEPT_FACE",FACE,{"disambiguationData":[OSD([subQ1])]});var subQ7=makeQuery(id+"F3.opExtrude","SWEPT_FACE",FACE,{"disambiguationData":[OSD([subQ1])]});var subQ8=sQuery(id+"F0.wireOp",EDGE,"E5");var subQ10=makeQuery(id+"F1.opExtrude","SWEPT_FACE",FACE,{"disambiguationData":[OSD([subQ1])]});var subQ11=sQuery(id+"F4.wireOp",EDGE,"E7");var subQ12=makeQuery(id+"F11.opExtrude","SWEPT_FACE",FACE,{"disambiguationData":[OSD([subQ1,subQ11])]});var subQ14=makeQuery(id+"F6.imprint","INTERSECT",VERTEX,{"derivedFrom":[makeQuery(id+"F5.opExtrude","CAP_EDGE",EDGE,{"disambiguationData":[OSD([subQ0])],"isStart":false}),subQ2]});var subQ15=makeQuery(id+"F7.opExtrude","SWEPT_FACE",FACE,{"disambiguationData":[OSD([subQ1,subQ0]),TDD([makeQuery(id+"F6.imprint","IMPRINT",EDGE,{"disambiguationData":[TD([[subQ14,1.0]])],"derivedFrom":subQ2})])]});var subQ16=sQuery(id+"F8.wireOp",EDGE,"E39.right");var subQ18=makeQuery(id+"F11.opExtrude","SWEPT_FACE",FACE,{"disambiguationData":[OSD([subQ16])]});Q0=makeQuery(id+"F13.boolean.opBoolean","SPLIT",FACE,{"disambiguationData":[TD([makeQuery(id+"F1.opExtrude","SWEPT_FACE",FACE,{"disambiguationData":[OSD([subQ8])]})])],"derivedFrom":makeQuery(id+"F11.boolean.opBoolean","MERGE",FACE,{"derivedFrom":[makeQuery(id+"F7.boolean.opBoolean","MERGE",FACE,{"derivedFrom":[makeQuery(id+"F5.boolean.opBoolean","MERGE",FACE,{"derivedFrom":[makeQuery(id+"F3.boolean.opBoolean","MERGE",FACE,{"derivedFrom":[subQ10,subQ7]}),subQ6]}),subQ5,subQ15]}),subQ18,subQ12]})});}
            var sketch = newSketch(context, id + "F26", { "sketchPlane" : qUnion([Q0])});
            skLineSegment(sketch, "E91", {"start": v(6.54, 36.2) * mm, "end": v(8.27, 33.2) * mm});
            skLineSegment(sketch, "E92", {"start": v(8.27, 33.2) * mm, "end": v(11.73, 33.2) * mm});
            skLineSegment(sketch, "E93", {"start": v(11.73, 33.2) * mm, "end": v(13.46, 36.2) * mm});
            skLineSegment(sketch, "E94", {"start": v(13.46, 36.2) * mm, "end": v(11.73, 39.2) * mm});
            skLineSegment(sketch, "E95", {"start": v(11.73, 39.2) * mm, "end": v(8.27, 39.2) * mm});
            skLineSegment(sketch, "E96", {"start": v(8.27, 39.2) * mm, "end": v(6.54, 36.2) * mm});
            skCircle(sketch, "E97", {"center": v(10, 36.2) * mm, "radius": 1.5 * mm});
            skLineSegment(sketch, "E98", {"start": v(6.54, 71.2) * mm, "end": v(8.27, 68.2) * mm});
            skLineSegment(sketch, "E99", {"start": v(8.27, 68.2) * mm, "end": v(11.73, 68.2) * mm});
            skLineSegment(sketch, "E100", {"start": v(11.73, 68.2) * mm, "end": v(13.46, 71.2) * mm});
            skLineSegment(sketch, "E101", {"start": v(13.46, 71.2) * mm, "end": v(11.73, 74.2) * mm});
            skLineSegment(sketch, "E102", {"start": v(11.73, 74.2) * mm, "end": v(8.27, 74.2) * mm});
            skLineSegment(sketch, "E103", {"start": v(8.27, 74.2) * mm, "end": v(6.54, 71.2) * mm});
            skCircle(sketch, "E104", {"center": v(10, 71.2) * mm, "radius": 1.5 * mm});
            skSolve(sketch);
        }
        {
            var Q0;
            Q0=makeQuery(id+"F26.imprint","IMPRINT",FACE,{"disambiguationData":[TD([[makeQuery(id+"F26.imprint","IMPRINT",EDGE,{"derivedFrom":sQuery(id+"F26.wireOp",EDGE,"E98")}),1.0]])]});
            var Q1;
            Q1=makeQuery(id+"F26.imprint","IMPRINT",FACE,{"disambiguationData":[TD([[makeQuery(id+"F26.imprint","IMPRINT",EDGE,{"derivedFrom":sQuery(id+"F26.wireOp",EDGE,"E91")}),1.0]])]});
            extrude(context, id + "F27", {"entities" : qUnion([Q0, Q1]), "operationType" : NewBodyOperationType.REMOVE, "oppositeDirection" : true, "depth" : 3 * mm, "offsetDistance" : 25 * mm});
        }
        {
            var Q0;
            Q0=sQuery(id+"F23.wireOp",VERTEX,"E89");
            var Q1;
            Q1=makeQuery(id+"F1.opExtrude","SWEPT_BODY",BODY,{"disambiguationData":[OSD([sQuery(id+"F0.wireOp",EDGE,"E0"),sQuery(id+"F0.wireOp",EDGE,"E1"),sQuery(id+"F0.wireOp",EDGE,"E2"),sQuery(id+"F0.wireOp",EDGE,"E3"),sQuery(id+"F0.wireOp",EDGE,"E4"),sQuery(id+"F0.wireOp",EDGE,"E5")])]});
            hole(context, id + "F28", {"style" : HoleStyle.C_BORE, "endStyle" : HoleEndStyle.THROUGH, "holeDiameter" : 3 * mm, "cBoreDiameter" : 6 * mm, "cBoreDepth" : 42 * mm, "isTappedThrough" : true, "tappedDepth" : 12 * mm, "tapClearance" : 3, "startFromSketch" : true, "locations" : qUnion([Q0]), "scope" : qUnion([Q1])});
        }
    });
